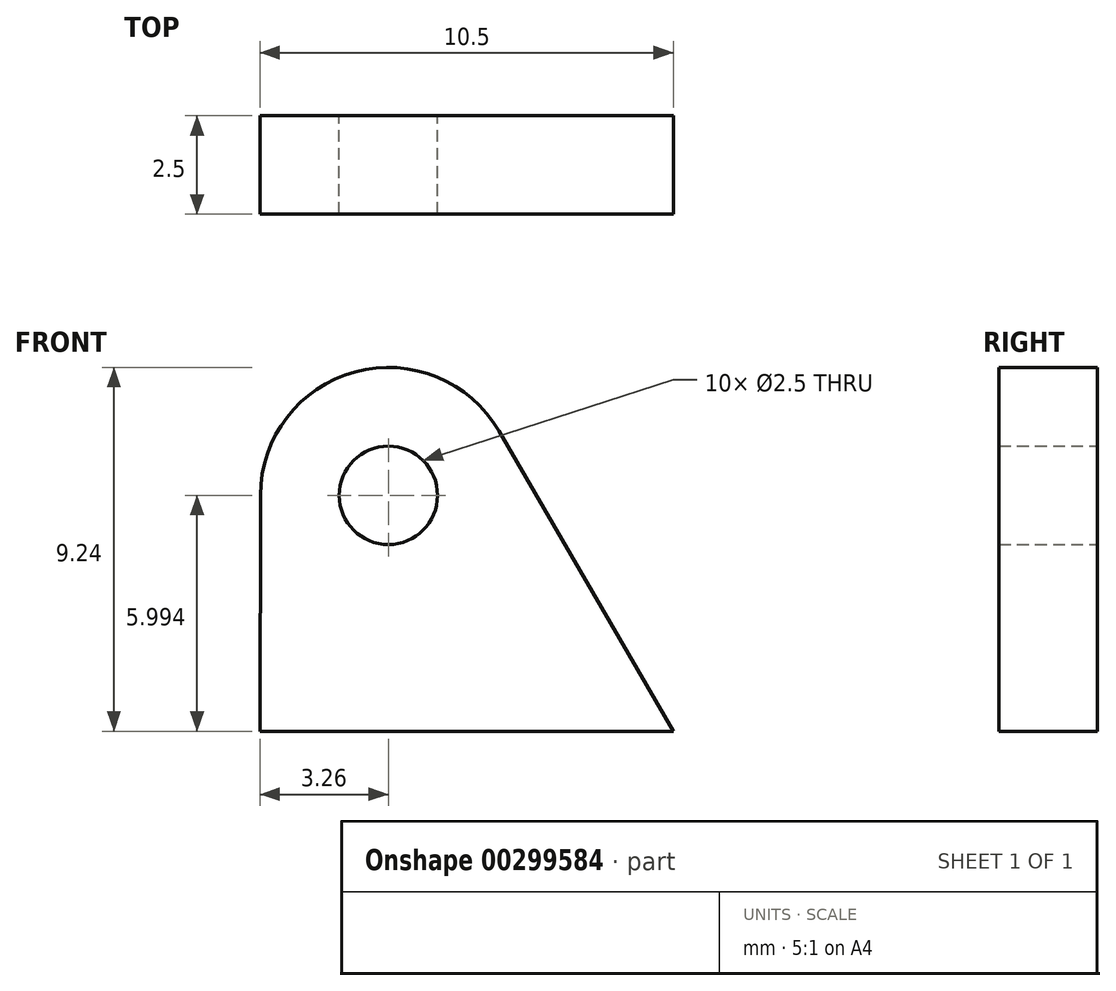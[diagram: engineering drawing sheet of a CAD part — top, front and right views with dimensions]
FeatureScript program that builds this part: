
annotation { "Feature Type Name" : "Feature", "Feature Type Description" : "" }
export const myFeature = defineFeature(function(context is Context, id is Id, definition is map)
    precondition{}
    {
        {
            var Q0;
            Q0=qCreatedBy(makeId("Front.planeOp"),FACE);
            var sketch = newSketch(context, id + "F0", { "sketchPlane" : qUnion([Q0])});
            skCircle(sketch, "E0", {"center": v(0, 8.45) * mm, "radius": 1.25 * mm});
            skCircle(sketch, "E1", {"center": v(0, 8.45) * mm, "radius": 3.25 * mm});
            skLineSegment(sketch, "E2", {"start": v(-3.25, 8.46) * mm, "end": v(-3.26, 2.46) * mm});
            skLineSegment(sketch, "E3", {"start": v(-3.26, 2.46) * mm, "end": v(7.24, 2.46) * mm});
            skLineSegment(sketch, "E4", {"start": v(7.24, 2.46) * mm, "end": v(2.81, 10.09) * mm});
            skSolve(sketch);
        }
        {
            var Q0;
            Q0 = qSketchRegion(id + "F0", true);
            extrude(context, id + "F1", {"entities" : qUnion([Q0]), "depth" : 2.5 * mm});
        }
    });
